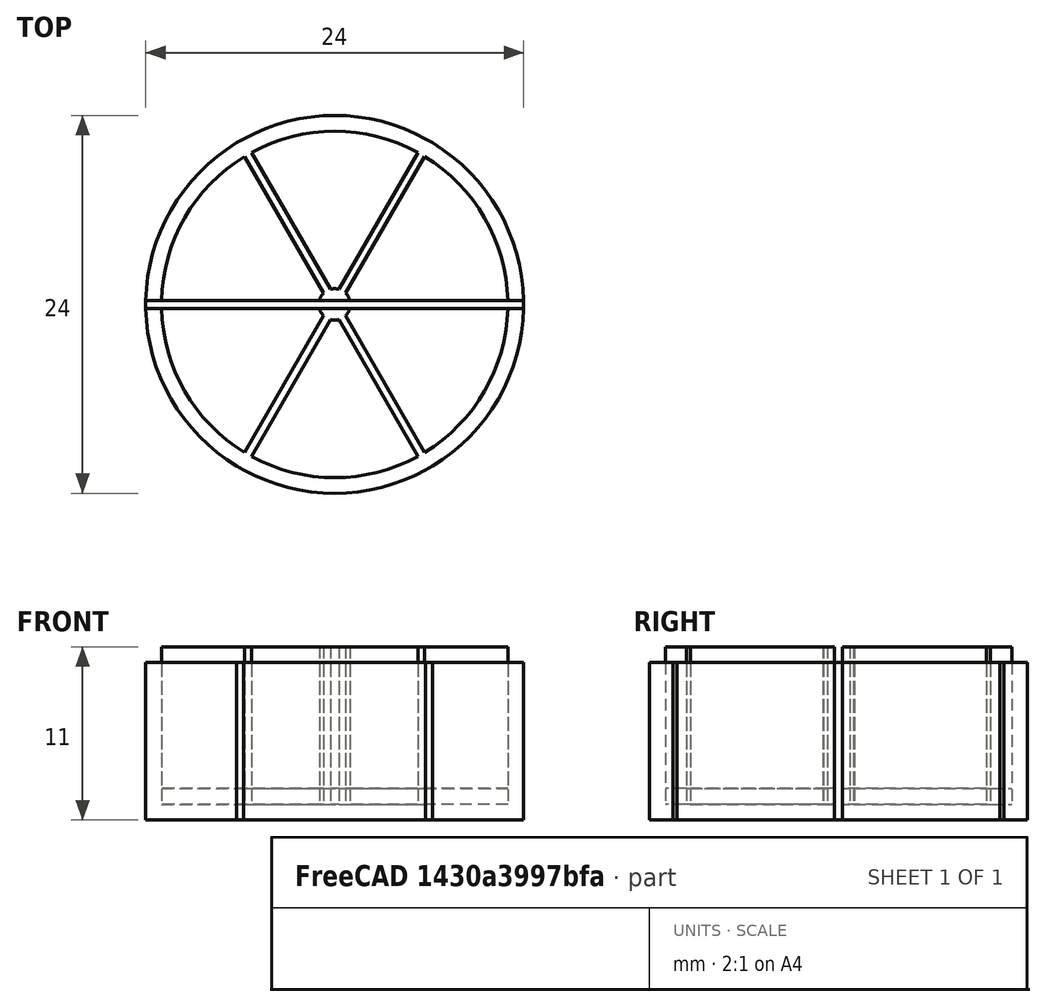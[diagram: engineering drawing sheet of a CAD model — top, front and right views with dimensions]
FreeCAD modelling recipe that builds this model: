
FCSTD DOCUMENT  (FreeCAD 1.0R39319 (Git))
Label: ojt1_t11r02_trivial
License: All rights reserved
LicenseURL: https://en.wikipedia.org/wiki/All_rights_reserved
objects: Part::Cylinder×7, Part::MultiFuse×6, Part::Cut×3, Part::Box×2, Part::FeaturePython×2
note: 18 computed .brp shape members not serialized (recipe doc carries the construction recipe); baked Part::Feature solids carry a one-line shape summary decoded from their .brp

FEATURE [Part::Cylinder] Cylinder
  Angle = 360
  AttacherType = Attacher::AttachEngine3D
  FirstAngle = 0
  Height = 10
  Radius = 12
  SecondAngle = 0
FEATURE [Part::Cylinder] Cylinder001
  Angle = 360
  AttacherType = Attacher::AttachEngine3D
  FirstAngle = 0
  Height = 9
  Placement = pos=(0,0,1) rot=(0,0,1;0rad)
  Radius = 11
  SecondAngle = 0
FEATURE [Part::Cut] Cut
  Base = -> Cylinder
  Refine = true
  Tool = -> Cylinder001
FEATURE [Part::Cylinder] Cylinder002
  Angle = 360
  AttacherType = Attacher::AttachEngine3D
  FirstAngle = 0
  Height = 10
  Radius = 1
  SecondAngle = 0
FEATURE [Part::MultiFuse] Fusion
  Refine = true
  Shapes = -> [Cylinder002,Cut]
FEATURE [Part::Box] Box  label="Cube"
  AttacherType = Attacher::AttachEngine3D
  Height = 10
  Length = 24
  Placement = pos=(-12,-0.25,0) rot=(0,0,1;0rad)
  Width = 0.5
FEATURE [Part::FeaturePython] Array  # Draft array (typed FeaturePython)
  AlwaysSyncPlacement = false
  Angle = 360
  ArrayType = 1
  Axis = (0,0,1)
  Base = -> Box
  Center = (0,0,0)
  Count = 3
  ExpandArray = false
  Fuse = false
  IntervalAxis = (0,0,0)
  IntervalX = (50,0,0)
  IntervalY = (0,50,0)
  IntervalZ = (0,0,50)
  NumberCircles = 3
  NumberPolar = 3
  NumberX = 2
  NumberY = 2
  NumberZ = 1
  PlacementList = 3 placements: [(-12,-0.25,0),(6.21651,-10.2673,0),(5.78349,10.5173,0)]
  RadialDistance = 50
  ScaleList = (3) [(1,1,1),(1,1,1),(1,1,1)]
  Symmetry = 1
  TangentialDistance = 25
FEATURE [Part::MultiFuse] Fusion001
  Refine = true
  Shapes = -> [Array]
FEATURE [Part::MultiFuse] Fusion002
  Refine = true
  Shapes = -> [Fusion,Fusion001]
FEATURE [Part::Cylinder] Cylinder003
  Angle = 360
  AttacherType = Attacher::AttachEngine3D
  FirstAngle = 0
  Height = 10
  Radius = 11
  SecondAngle = 0
FEATURE [Part::Box] Box001  label="Cube001"
  AttacherType = Attacher::AttachEngine3D
  Height = 10
  Length = 24
  Placement = pos=(-12,-0.25,0) rot=(0,0,1;0rad)
  Width = 0.5
FEATURE [Part::FeaturePython] Array001  # Draft array (typed FeaturePython)
  AlwaysSyncPlacement = false
  Angle = 360
  ArrayType = 1
  Axis = (0,0,1)
  Base = -> Box001
  Center = (0,0,0)
  Count = 3
  ExpandArray = false
  Fuse = false
  IntervalAxis = (0,0,0)
  IntervalX = (50,0,0)
  IntervalY = (0,50,0)
  IntervalZ = (0,0,50)
  NumberCircles = 3
  NumberPolar = 3
  NumberX = 2
  NumberY = 2
  NumberZ = 1
  PlacementList = 3 placements: [(-12,-0.25,0),(6.21651,-10.2673,0),(5.78349,10.5173,0)]
  RadialDistance = 50
  ScaleList = (3) [(1,1,1),(1,1,1),(1,1,1)]
  Symmetry = 1
  TangentialDistance = 25
FEATURE [Part::Cylinder] Cylinder004
  Angle = 360
  AttacherType = Attacher::AttachEngine3D
  FirstAngle = 0
  Height = 10
  Radius = 12
  SecondAngle = 0
FEATURE [Part::Cylinder] Cylinder005
  Angle = 360
  AttacherType = Attacher::AttachEngine3D
  FirstAngle = 0
  Height = 9
  Placement = pos=(0,0,1) rot=(0,0,1;0rad)
  Radius = 11
  SecondAngle = 0
FEATURE [Part::Cut] Cut001
  Base = -> Cylinder004
  Refine = true
  Tool = -> Cylinder005
FEATURE [Part::Cylinder] Cylinder006
  Angle = 360
  AttacherType = Attacher::AttachEngine3D
  FirstAngle = 0
  Height = 10
  Radius = 1
  SecondAngle = 0
FEATURE [Part::MultiFuse] Fusion003
  Refine = true
  Shapes = -> [Cylinder006,Cut001]
FEATURE [Part::MultiFuse] Fusion004
  Refine = true
  Shapes = -> [Array001]
FEATURE [Part::MultiFuse] Fusion005
  Refine = true
  Shapes = -> [Fusion003,Fusion004]
FEATURE [Part::Cut] Cut002
  Base = -> Cylinder003
  Placement = pos=(0,0,1) rot=(0,0,1;0rad)
  Refine = true
  Tool = -> Fusion005
